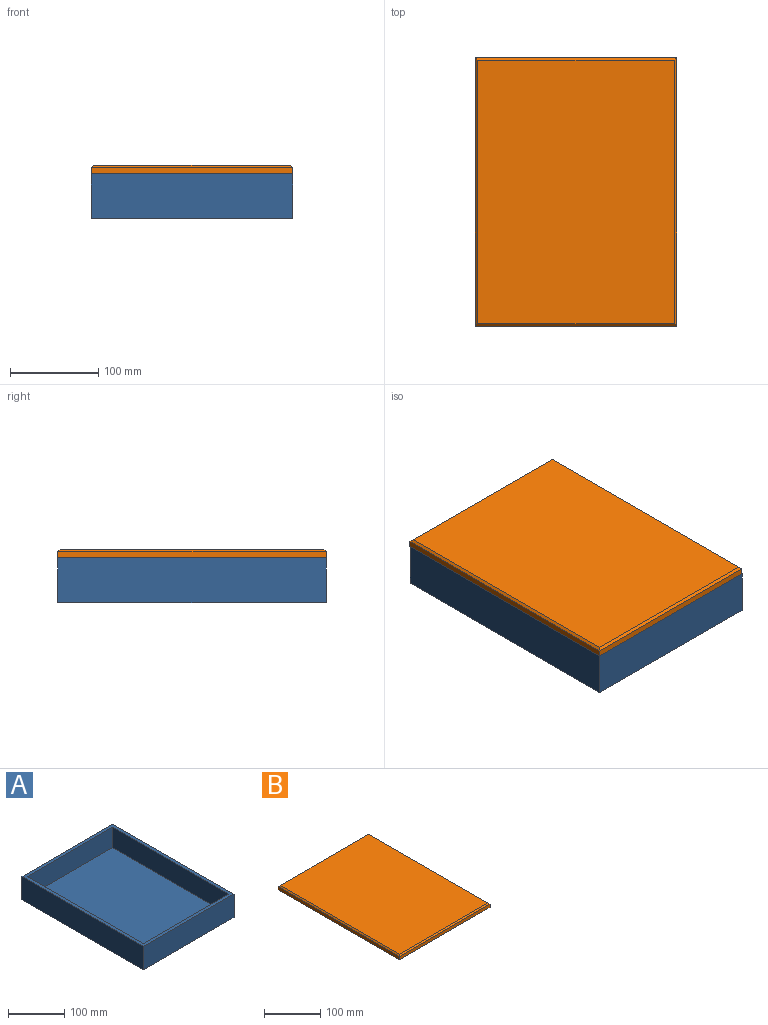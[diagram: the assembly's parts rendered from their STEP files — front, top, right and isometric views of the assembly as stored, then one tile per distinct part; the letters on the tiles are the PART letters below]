
ASSEMBLY  parts=2 mates=1
PART A: 11 faces, bbox 228.6x304.8x50.8 mm
  f0: plane 228.6x50.8mm, normal (0,1,0), area 11612.9mm2, adj f1,f7,f8,f9
  f1: plane 304.8x50.8mm, normal (-1,0,0), area 15483.8mm2, adj f0,f2,f8,f9
  f2: plane 228.6x50.8mm, normal (0,-1,0), area 11612.9mm2, adj f1,f7,f8,f9
  f3: plane 215.9x44.45mm, normal (0,-1,0), area 9596.8mm2, adj f4,f6,f8,f10
  f4: plane 292.1x44.45mm, normal (-1,0,0), area 12983.8mm2, adj f3,f5,f8,f10
  f5: plane 215.9x44.45mm, normal (0,1,0), area 9596.8mm2, adj f4,f6,f8,f10
  f6: plane 292.1x44.45mm, normal (1,0,0), area 12983.8mm2, adj f3,f5,f8,f10
  f7: plane 304.8x50.8mm, normal (1,0,0), area 15483.8mm2, adj f0,f2,f8,f9
  f8: plane 304.8x228.6mm, normal (0,0,1), area 6612.9mm2, adj f0,f1,f2,f3,f4,f5,f6,f7
  f9: plane 304.8x228.6mm, normal (0,0,-1), area 69677.3mm2, adj f0,f1,f2,f7
  f10: plane 292.1x215.9mm, normal (0,0,1), area 63064.4mm2, adj f3,f4,f5,f6
PART B: 15 faces, bbox 228.6x304.8x9.5 mm
  f0: plane 304.8x228.6mm, normal (0,0,-1), area 6612.9mm2, adj f1,f2,f3,f4,f11,f12,f13,f14
  f1: plane 304.8x6.99mm, normal (-1,0,0), area 2129mm2, adj f0,f2,f4,f6
  f2: plane 228.6x6.99mm, normal (0,-1,0), area 1596.8mm2, adj f0,f1,f3,f7
  f3: plane 304.8x6.99mm, normal (1,0,0), area 2129mm2, adj f0,f2,f4,f9
  f4: plane 228.6x6.99mm, normal (0,1,0), area 1596.8mm2, adj f0,f1,f3,f8
  f5: plane 299.72x223.52mm, normal (0,0,1), area 66993.4mm2, adj f6,f7,f8,f9
  f6: plane 304.8x2.54mm, normal (-0.71,0,0.71), area 1085.7mm2, adj f1,f5,f7,f8
  f7: plane 228.6x2.54mm, normal (0,-0.71,0.71), area 812mm2, adj f2,f5,f6,f9
  f8: plane 228.6x2.54mm, normal (0,0.71,0.71), area 812mm2, adj f4,f5,f6,f9
  f9: plane 304.8x2.54mm, normal (0.71,0,0.71), area 1085.7mm2, adj f3,f5,f7,f8
  f10: plane 292.1x215.9mm, normal (0,0,-1), area 63064.4mm2, adj f11,f12,f13,f14
  f11: plane 292.1x3.18mm, normal (1,0,0), area 927.4mm2, adj f0,f10,f12,f14
  f12: plane 215.9x3.18mm, normal (0,1,0), area 685.5mm2, adj f0,f10,f11,f13
  f13: plane 292.1x3.18mm, normal (-1,0,0), area 927.4mm2, adj f0,f10,f12,f14
  f14: plane 215.9x3.18mm, normal (0,-1,0), area 685.5mm2, adj f0,f10,f11,f13
PLACE A t=(-101.84,-10.34,-86.24)mm
PLACE B t=(376.29,-687,-35.44)mm
MATE revolute B.f0 <-> A.f8  axis (0,0,-1) through (-350.64,-79.54,-35.44)mm
